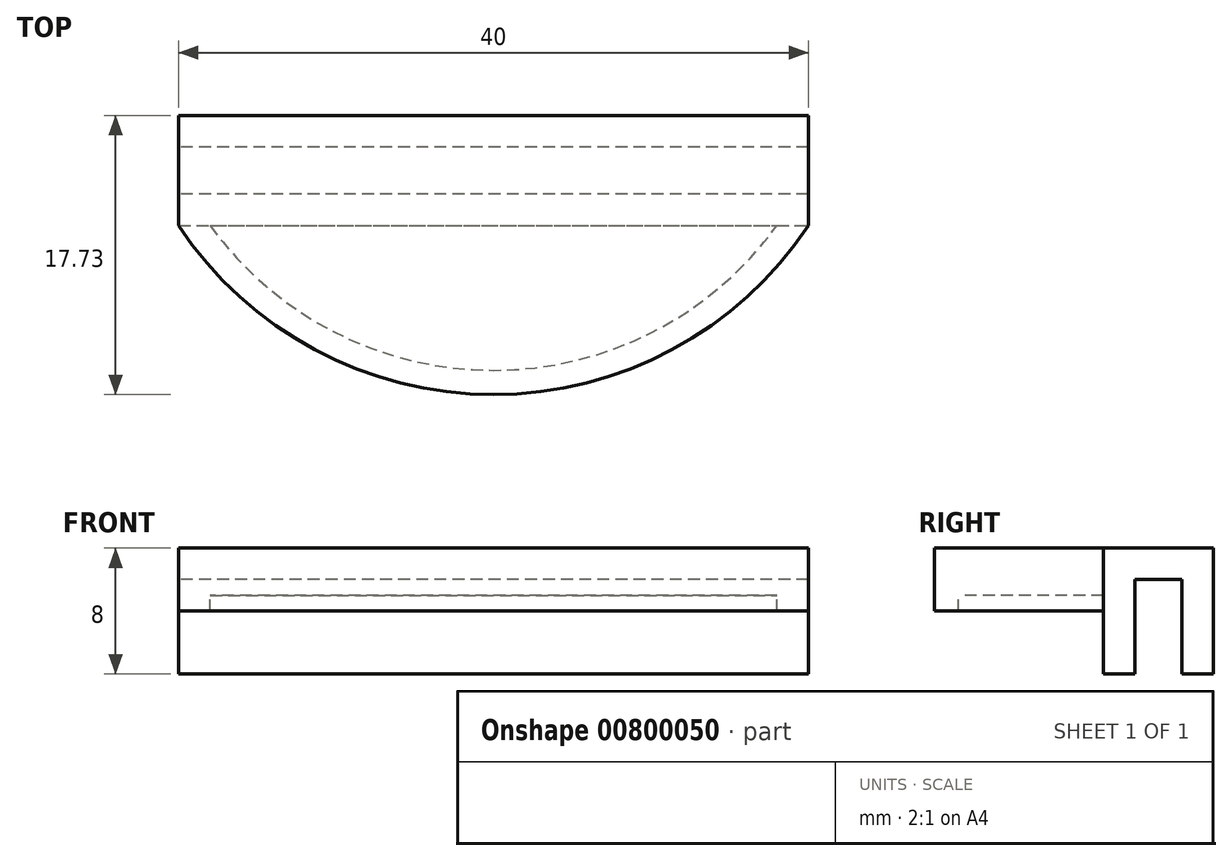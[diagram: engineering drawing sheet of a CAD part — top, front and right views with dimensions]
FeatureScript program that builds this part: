
annotation { "Feature Type Name" : "Feature", "Feature Type Description" : "" }
export const myFeature = defineFeature(function(context is Context, id is Id, definition is map)
    precondition{}
    {
        {
            var Q0;
            Q0=qCreatedBy(makeId("Top.planeOp"),FACE);
            var sketch = newSketch(context, id + "F0", { "sketchPlane" : qUnion([Q0])});
            skLineSegment(sketch, "E0.bottom", {"start": v(-19.61, 2) * mm, "end": v(20.39, 2) * mm});
            skLineSegment(sketch, "E0.top", {"start": v(-19.61, 0) * mm, "end": v(20.39, 0) * mm});
            skLineSegment(sketch, "E0.left", {"start": v(-19.61, 2) * mm, "end": v(-19.61, 0) * mm});
            skLineSegment(sketch, "E0.right", {"start": v(20.39, 2) * mm, "end": v(20.39, 0) * mm});
            skArc(sketch, "E1", {"start": v(-19.61, 0) * mm, "mid": v(0.39, -10.73) * mm, "end": v(20.39, 0) * mm});
            skSolve(sketch);
        }
        {
            var Q0;
            Q0=makeQuery(id+"F0.imprint","IMPRINT",FACE,{"disambiguationData":[TD([[makeQuery(id+"F0.imprint","IMPRINT",EDGE,{"derivedFrom":sQuery(id+"F0.wireOp",EDGE,"E0.bottom")}),-1.0]])]});
            extrude(context, id + "F1", {"entities" : qUnion([Q0]), "oppositeDirection" : true, "depth" : 8 * mm, "offsetDistance" : 25 * mm});
        }
        {
            var Q0;
            Q0=makeQuery(id+"F0.imprint","IMPRINT",FACE,{"disambiguationData":[TD([[makeQuery(id+"F0.imprint","IMPRINT",EDGE,{"derivedFrom":sQuery(id+"F0.wireOp",EDGE,"E0.top")}),-1.0]])]});
            extrude(context, id + "F2", {"entities" : qUnion([Q0]), "operationType" : NewBodyOperationType.ADD, "oppositeDirection" : true, "depth" : 3 * mm, "offsetDistance" : 25 * mm});
        }
        {
            var Q0;
            Q0=makeQuery(id+"F2.opExtrude","CAP_FACE",FACE,{"disambiguationData":[OSD([sQuery(id+"F0.wireOp",EDGE,"E0.top"),sQuery(id+"F0.wireOp",EDGE,"E1")])],"isStart":false});
            var sketch = newSketch(context, id + "F3", { "sketchPlane" : qUnion([Q0])});
            skArc(sketch, "E2", {"start": v(20.39, 0) * mm, "mid": v(0.39, 10.73) * mm, "end": v(-19.61, 0) * mm});
            skArc(sketch, "E3", {"start": v(18.39, 0) * mm, "mid": v(0.39, 9.19) * mm, "end": v(-17.61, 0) * mm});
            skLineSegment(sketch, "E4", {"start": v(-17.61, 0) * mm, "end": v(-19.61, 0) * mm});
            skLineSegment(sketch, "E5", {"start": v(18.39, 0) * mm, "end": v(20.39, 0) * mm});
            skSolve(sketch);
        }
        {
            var Q0;
            Q0=makeQuery(id+"F3.imprint","IMPRINT",FACE,{"disambiguationData":[TD([[makeQuery(id+"F3.imprint","IMPRINT",EDGE,{"derivedFrom":sQuery(id+"F3.wireOp",EDGE,"E2")}),-1.0]])]});
            extrude(context, id + "F4", {"entities" : qUnion([Q0]), "operationType" : NewBodyOperationType.ADD, "depth" : 1 * mm, "offsetDistance" : 25 * mm});
        }
        {
            var Q0;
            Q0=makeQuery(id+"F1.opExtrude","SWEPT_FACE",FACE,{"disambiguationData":[OSD([sQuery(id+"F0.wireOp",EDGE,"E0.bottom")])]});
            var sketch = newSketch(context, id + "F5", { "sketchPlane" : qUnion([Q0])});
            skLineSegment(sketch, "E6.bottom", {"start": v(-20.39, 0) * mm, "end": v(19.61, 0) * mm});
            skLineSegment(sketch, "E6.top", {"start": v(-20.39, -2) * mm, "end": v(19.61, -2) * mm});
            skLineSegment(sketch, "E6.left", {"start": v(-20.39, 0) * mm, "end": v(-20.39, -2) * mm});
            skLineSegment(sketch, "E6.right", {"start": v(19.61, 0) * mm, "end": v(19.61, -2) * mm});
            skSolve(sketch);
        }
        {
            var Q0;
            Q0=makeQuery(id+"F5.imprint","IMPRINT",FACE,{"disambiguationData":[TD([[makeQuery(id+"F5.imprint","IMPRINT",EDGE,{"derivedFrom":sQuery(id+"F5.wireOp",EDGE,"E6.bottom")}),1.0]])]});
            extrude(context, id + "F6", {"entities" : qUnion([Q0]), "operationType" : NewBodyOperationType.ADD, "depth" : 3 * mm, "offsetDistance" : 25 * mm});
        }
        {
            var Q0;
            Q0=makeQuery(id+"F6.opExtrude","CAP_FACE",FACE,{"disambiguationData":[OSD([sQuery(id+"F5.wireOp",EDGE,"E6.bottom"),sQuery(id+"F5.wireOp",EDGE,"E6.top"),sQuery(id+"F5.wireOp",EDGE,"E6.left"),sQuery(id+"F5.wireOp",EDGE,"E6.right")])],"isStart":false});
            var sketch = newSketch(context, id + "F7", { "sketchPlane" : qUnion([Q0])});
            skLineSegment(sketch, "E7.bottom", {"start": v(-20.39, 0) * mm, "end": v(19.61, 0) * mm});
            skLineSegment(sketch, "E7.top", {"start": v(-20.39, -8) * mm, "end": v(19.61, -8) * mm});
            skLineSegment(sketch, "E7.left", {"start": v(-20.39, 0) * mm, "end": v(-20.39, -8) * mm});
            skLineSegment(sketch, "E7.right", {"start": v(19.61, 0) * mm, "end": v(19.61, -8) * mm});
            skSolve(sketch);
        }
        {
            var Q0;
            {var subQ0=sQuery(id+"F7.wireOp",EDGE,"E7.top");Q0=makeQuery(id+"F7.imprint","IMPRINT",FACE,{"disambiguationData":[TD([[makeQuery(id+"F7.imprint","IMPRINT",EDGE,{"derivedFrom":subQ0}),1.0]])]});}
            var Q1;
            {var subQ0=sQuery(id+"F7.wireOp",EDGE,"E7.bottom");Q1=makeQuery(id+"F7.imprint","IMPRINT",FACE,{"disambiguationData":[TD([[makeQuery(id+"F7.imprint","IMPRINT",EDGE,{"derivedFrom":subQ0}),1.0]])]});}
            extrude(context, id + "F8", {"entities" : qUnion([Q0, Q1]), "operationType" : NewBodyOperationType.ADD, "depth" : 2 * mm, "offsetDistance" : 25 * mm});
        }
    });
